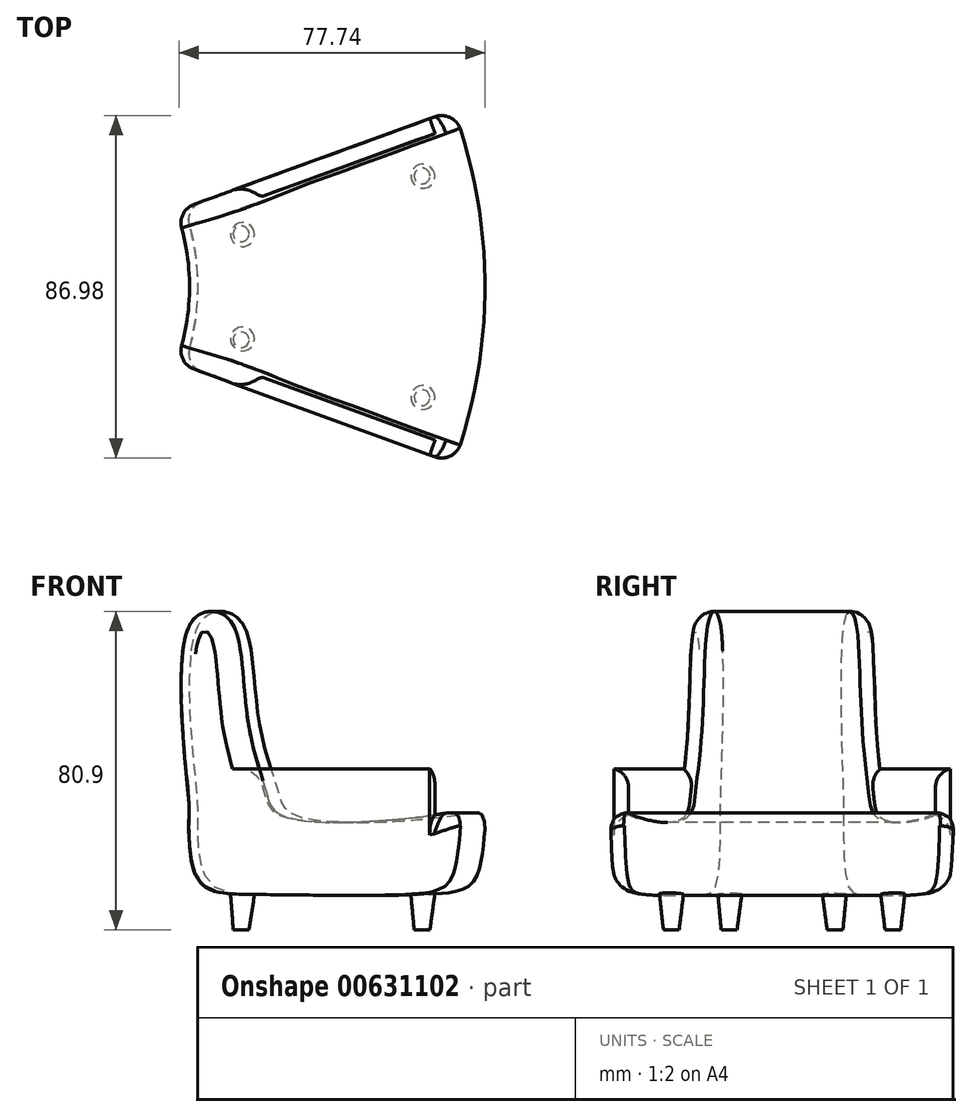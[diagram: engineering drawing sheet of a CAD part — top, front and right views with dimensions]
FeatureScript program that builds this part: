
annotation { "Feature Type Name" : "Feature", "Feature Type Description" : "" }
export const myFeature = defineFeature(function(context is Context, id is Id, definition is map)
    precondition{}
    {
        {
            var Q0;
            Q0=qCreatedBy(makeId("Front.planeOp"),FACE);
            var sketch = newSketch(context, id + "F0", { "sketchPlane" : qUnion([Q0])});
            skFitSpline(sketch, "E0", {"points": [v(-40.73, 0) * mm, v(-41, 6.47) * mm, v(-40.83, 47.94) * mm, v(-33.3, 51.68) * mm, v(-28.34, 46.6) * mm, v(-25.07, 23.17) * mm, v(-20.27, 6.16) * mm, v(-15.88, 0) * mm, v(24.13, 0) * mm, v(31.62, 0) * mm, v(31.62, -8.5) * mm, v(28.58, -17.45) * mm, v(17.83, -19.97) * mm, v(0, -20.22) * mm, v(-25.48, -19.97) * mm, v(-38.32, -16.3) * mm, v(-40.73, 0) * mm]});
            skSolve(sketch);
        }
        {
            var Q0;
            Q0=qCreatedBy(makeId("Top.planeOp"),FACE);
            cPlane(context, id + "F1", {"entities" : qUnion([Q0]), "cplaneType" : CPlaneType.OFFSET, "offset" : 16 * mm, "oppositeDirection" : true, "width" : 150 * mm, "height" : 150 * mm});
        }
        {
            var Q0;
            Q0=qCreatedBy(id+"F1.planeOp",FACE);
            var sketch = newSketch(context, id + "F2", { "sketchPlane" : qUnion([Q0])});
            skCircle(sketch, "E1", {"center": v(-99.25, 0) * mm, "radius": 56.84 * mm});
            skSolve(sketch);
        }
        {
            var Q0;
            Q0=qSketchRegion(id+"F0",true);
            var Q1;
            Q1=sQuery(id+"F2.wireOp",EDGE,"E1");
            revolve(context, id + "F3", {"entities" : qUnion([Q0]), "axis" : qUnion([Q1]), "revolveType" : RevolveType.SYMMETRIC, "oppositeDirection" : true, "angle" : 40 * degree});
        }
        {
            var Q0;
            Q0=makeQuery(id+"F3.opRevolve","CAP_EDGE",EDGE,{"disambiguationData":[OSD([sQuery(id+"F0.wireOp",EDGE,"E0")])],"isStart":false});
            fillet(context, id + "F4", {"entities" : qUnion([Q0]), "radius" : 5 * mm, "tangentPropagation" : true, "allowEdgeOverflow" : false});
        }
        {
            var Q0;
            Q0=makeQuery(id+"F3.opRevolve","CAP_EDGE",EDGE,{"disambiguationData":[OSD([sQuery(id+"F0.wireOp",EDGE,"E0")])],"isStart":true});
            fillet(context, id + "F5", {"entities" : qUnion([Q0]), "radius" : 5 * mm, "tangentPropagation" : true, "allowEdgeOverflow" : false});
        }
        {
            var Q0;
            Q0=makeQuery(id+"F3.opRevolve","CAP_FACE",FACE,{"disambiguationData":[OSD([sQuery(id+"F0.wireOp",EDGE,"E0")])],"isStart":false});
            cPlane(context, id + "F6", {"entities" : qUnion([Q0]), "cplaneType" : CPlaneType.OFFSET, "offset" : 0 * mm, "width" : 150 * mm, "height" : 150 * mm});
        }
        {
            var Q0;
            Q0=qCreatedBy(id+"F6.planeOp",FACE);
            var sketch = newSketch(context, id + "F7", { "sketchPlane" : qUnion([Q0])});
            skLineSegment(sketch, "E2.bottom", {"start": v(-25.15, 11.93) * mm, "end": v(31.65, 11.93) * mm});
            skLineSegment(sketch, "E2.top", {"start": v(-25.15, -10.4) * mm, "end": v(31.65, -10.4) * mm});
            skLineSegment(sketch, "E2.left", {"start": v(-25.15, 11.93) * mm, "end": v(-25.15, -10.4) * mm});
            skLineSegment(sketch, "E2.right", {"start": v(31.65, 11.93) * mm, "end": v(31.65, -10.4) * mm});
            skSolve(sketch);
        }
        {
            var Q0;
            Q0=makeQuery(id+"F7.imprint","IMPRINT",FACE,{"disambiguationData":[TD([[makeQuery(id+"F7.imprint","IMPRINT",EDGE,{"derivedFrom":sQuery(id+"F7.wireOp",EDGE,"E2.bottom")}),-1.0]])]});
            extrude(context, id + "F8", {"entities" : qUnion([Q0]), "oppositeDirection" : true, "depth" : 4 * mm, "offsetDistance" : 25 * mm});
        }
        {
            var Q0;
            Q0=makeQuery(id+"F8.opExtrude","CAP_EDGE",EDGE,{"disambiguationData":[OSD([sQuery(id+"F7.wireOp",EDGE,"E2.bottom")])],"isStart":false});
            fillet(context, id + "F9", {"entities" : qUnion([Q0]), "radius" : 5 * mm, "tangentPropagation" : true, "allowEdgeOverflow" : false});
        }
        {
            var Q0;
            Q0=makeQuery(id+"F8.opExtrude","SWEPT_BODY",BODY,{"disambiguationData":[OSD([sQuery(id+"F7.wireOp",EDGE,"E2.bottom"),sQuery(id+"F7.wireOp",EDGE,"E2.top"),sQuery(id+"F7.wireOp",EDGE,"E2.left"),sQuery(id+"F7.wireOp",EDGE,"E2.right")])]});
            var Q1;
            Q1=qCreatedBy(makeId("Front.planeOp"),FACE);
            mirror(context, id + "F10", {"operationType" : NewBodyOperationType.ADD, "entities" : qUnion([Q0]), "mirrorPlane" : qUnion([Q1])});
        }
        {
            var Q0;
            Q0=qCreatedBy(id+"F1.planeOp",FACE);
            cPlane(context, id + "F11", {"entities" : qUnion([Q0]), "cplaneType" : CPlaneType.OFFSET, "offset" : 13 * mm, "oppositeDirection" : true, "width" : 150 * mm, "height" : 150 * mm});
        }
        {
            var Q0;
            Q0=qCreatedBy(id+"F1.planeOp",FACE);
            var sketch = newSketch(context, id + "F12", { "sketchPlane" : qUnion([Q0])});
            skCircle(sketch, "E3", {"center": v(-29.25, 13.2) * mm, "radius": 3.5 * mm});
            skSolve(sketch);
        }
        {
            var Q0;
            Q0=qCreatedBy(id+"F11.planeOp",FACE);
            var sketch = newSketch(context, id + "F13", { "sketchPlane" : qUnion([Q0])});
            skCircle(sketch, "E4", {"center": v(-29.77, 13.45) * mm, "radius": 2 * mm});
            skSolve(sketch);
        }
        {
            var Q1;
            Q1 = qSketchRegion(id + "F12", true);
            var Q2;
            Q2 = qSketchRegion(id + "F13", true);
            loft(context, id + "F14", {"sheetProfilesArray" : [{ "sheetProfileEntities" : qUnion([Q1]) }, { "sheetProfileEntities" : qUnion([Q2]) }]});
        }
        {
            var Q0;
            Q0=makeQuery(id+"F14.opLoft","SWEPT_BODY",BODY,{"disambiguationData":[OSD([makeQuery(id+"F12.imprint","IMPRINT",FACE,{"disambiguationData":[TD([[makeQuery(id+"F12.imprint","IMPRINT",EDGE,{"derivedFrom":sQuery(id+"F12.wireOp",EDGE,"E3")}),1.0]])]}),makeQuery(id+"F13.imprint","IMPRINT",FACE,{"disambiguationData":[TD([[makeQuery(id+"F13.imprint","IMPRINT",EDGE,{"derivedFrom":sQuery(id+"F13.wireOp",EDGE,"E4")}),1.0]])]})])]});
            var Q1;
            Q1=qCreatedBy(makeId("Front.planeOp"),FACE);
            mirror(context, id + "F15", {"operationType" : NewBodyOperationType.ADD, "entities" : qUnion([Q0]), "mirrorPlane" : qUnion([Q1])});
        }
        {
            var Q0;
            Q0=qCreatedBy(id+"F1.planeOp",FACE);
            var sketch = newSketch(context, id + "F16", { "sketchPlane" : qUnion([Q0])});
            skCircle(sketch, "E5", {"center": v(16.46, 28.08) * mm, "radius": 3.5 * mm});
            skSolve(sketch);
        }
        {
            var Q0;
            Q0=qCreatedBy(id+"F11.planeOp",FACE);
            var sketch = newSketch(context, id + "F17", { "sketchPlane" : qUnion([Q0])});
            skCircle(sketch, "E6", {"center": v(16.2, 28.15) * mm, "radius": 2 * mm});
            skSolve(sketch);
        }
        {
            var Q1;
            Q1 = qSketchRegion(id + "F16", true);
            var Q2;
            Q2 = qSketchRegion(id + "F17", true);
            loft(context, id + "F18", {"sheetProfilesArray" : [{ "sheetProfileEntities" : qUnion([Q1]) }, { "sheetProfileEntities" : qUnion([Q2]) }]});
        }
        {
            var Q0;
            Q0=makeQuery(id+"F18.opLoft","SWEPT_BODY",BODY,{"disambiguationData":[OSD([makeQuery(id+"F16.imprint","IMPRINT",FACE,{"disambiguationData":[TD([[makeQuery(id+"F16.imprint","IMPRINT",EDGE,{"derivedFrom":sQuery(id+"F16.wireOp",EDGE,"E5")}),1.0]])]}),makeQuery(id+"F17.imprint","IMPRINT",FACE,{"disambiguationData":[TD([[makeQuery(id+"F17.imprint","IMPRINT",EDGE,{"derivedFrom":sQuery(id+"F17.wireOp",EDGE,"E6")}),1.0]])]})])]});
            var Q1;
            Q1=qCreatedBy(makeId("Front.planeOp"),FACE);
            mirror(context, id + "F19", {"operationType" : NewBodyOperationType.ADD, "entities" : qUnion([Q0]), "mirrorPlane" : qUnion([Q1])});
        }
    });
